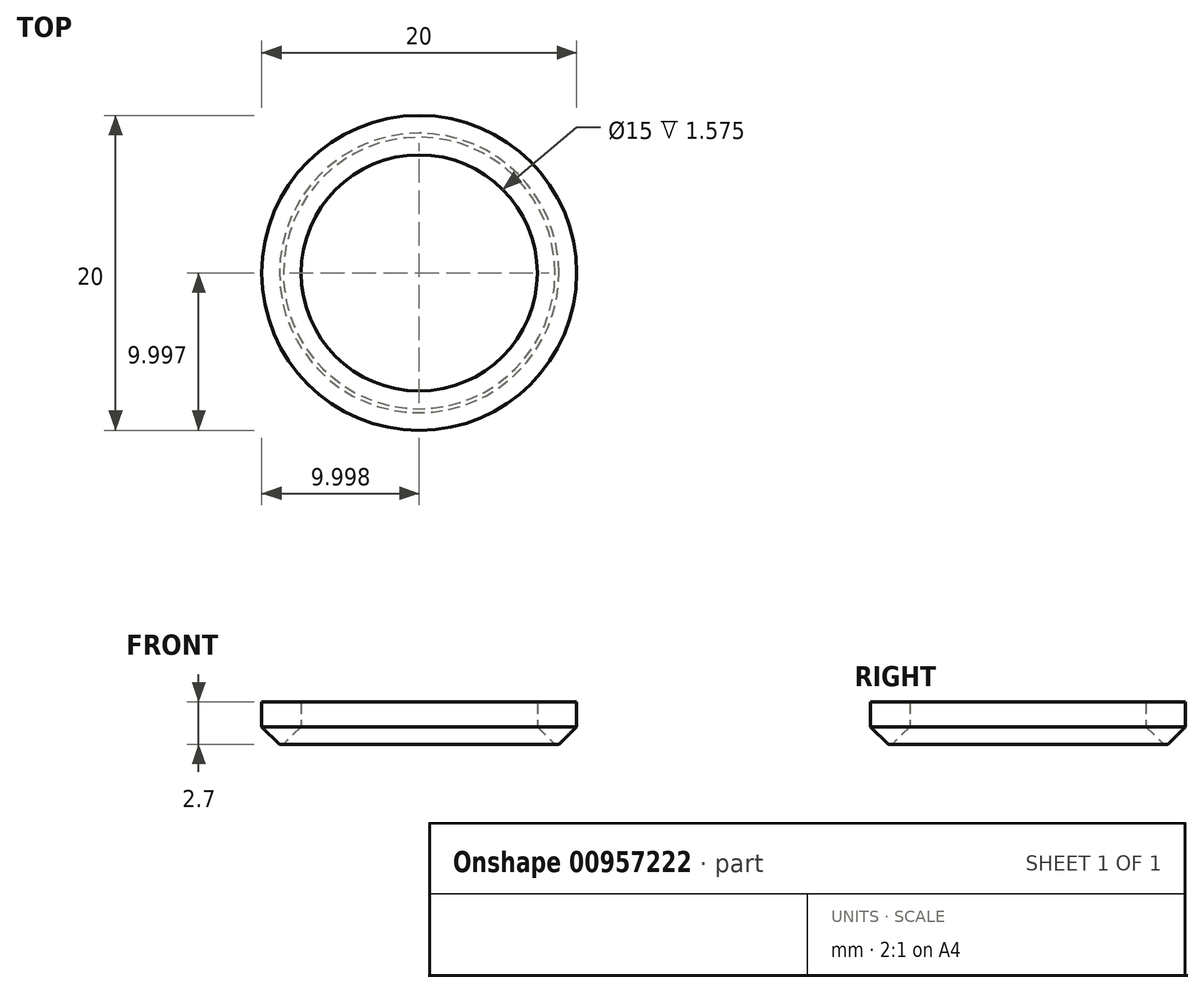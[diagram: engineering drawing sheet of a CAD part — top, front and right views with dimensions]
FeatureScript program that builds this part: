
annotation { "Feature Type Name" : "Feature", "Feature Type Description" : "" }
export const myFeature = defineFeature(function(context is Context, id is Id, definition is map)
    precondition{}
    {
        {
            var Q0;
            Q0=qCreatedBy(makeId("Top.planeOp"),FACE);
            var sketch = newSketch(context, id + "F0", { "sketchPlane" : qUnion([Q0])});
            skCircle(sketch, "E0", {"center": v(-21.36, 22.82) * mm, "radius": 7.5 * mm});
            skCircle(sketch, "E1", {"center": v(-21.36, 22.82) * mm, "radius": 10 * mm});
            skCircle(sketch, "E2", {"center": v(-21.36, 22.82) * mm, "radius": 8.62 * mm});
            skCircle(sketch, "E3", {"center": v(-21.36, 22.82) * mm, "radius": 8.88 * mm});
            skSolve(sketch);
        }
        {
            var Q0;
            Q0=makeQuery(id+"F0.imprint","IMPRINT",FACE,{"disambiguationData":[TD([[makeQuery(id+"F0.imprint","IMPRINT",EDGE,{"derivedFrom":sQuery(id+"F0.wireOp",EDGE,"E2")}),-1.0]])]});
            extrude(context, id + "F1", {"entities" : qUnion([Q0]), "depth" : 3 * mm, "offsetDistance" : 25 * mm, "hasDraft" : true, "draftAngle" : 45 * degree});
        }
        {
            var Q0;
            Q0=makeQuery(id+"F0.imprint","IMPRINT",FACE,{"disambiguationData":[TD([[makeQuery(id+"F0.imprint","IMPRINT",EDGE,{"derivedFrom":sQuery(id+"F0.wireOp",EDGE,"E0")}),-1.0]])]});
            var Q1;
            Q1=makeQuery(id+"F0.imprint","IMPRINT",FACE,{"disambiguationData":[TD([[makeQuery(id+"F0.imprint","IMPRINT",EDGE,{"derivedFrom":sQuery(id+"F0.wireOp",EDGE,"E1")}),1.0]])]});
            var Q2;
            Q2=makeQuery(id+"F0.imprint","IMPRINT",FACE,{"disambiguationData":[TD([[makeQuery(id+"F0.imprint","IMPRINT",EDGE,{"derivedFrom":sQuery(id+"F0.wireOp",EDGE,"E2")}),-1.0]])]});
            extrude(context, id + "F2", {"entities" : qUnion([Q0, Q1, Q2]), "operationType" : NewBodyOperationType.INTERSECT, "depth" : 2.7 * mm, "offsetDistance" : 25 * mm});
        }
    });
